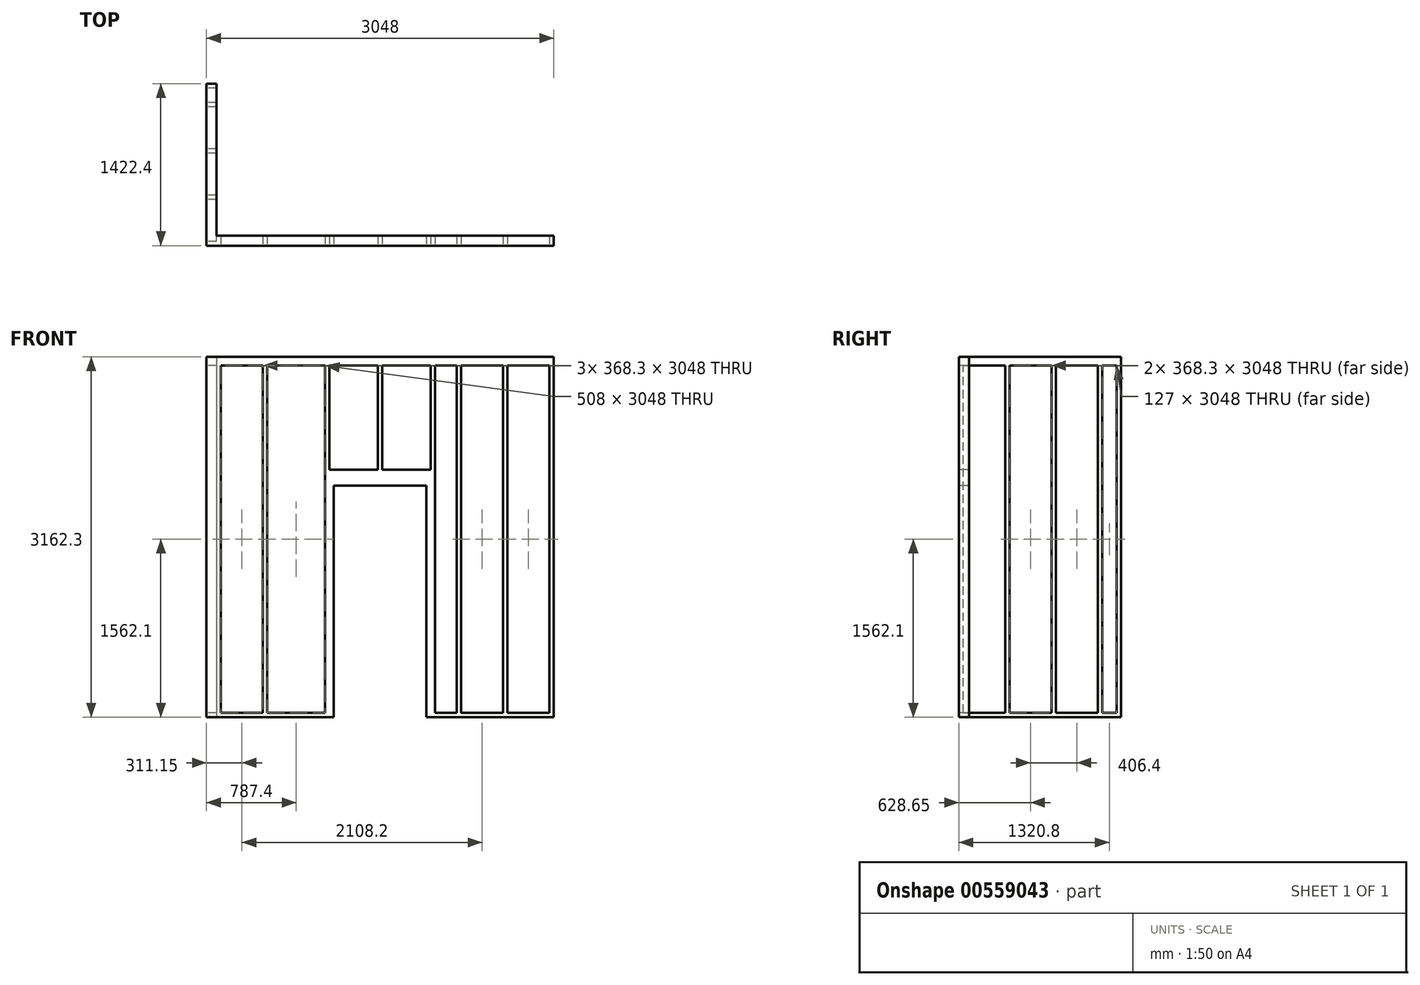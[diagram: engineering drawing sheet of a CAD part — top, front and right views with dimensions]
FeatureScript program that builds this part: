
annotation { "Feature Type Name" : "Feature", "Feature Type Description" : "" }
export const myFeature = defineFeature(function(context is Context, id is Id, definition is map)
    precondition{}
    {
        {
            var Q0;
            Q0=qCreatedBy(makeId("Top.planeOp"),FACE);
            var sketch = newSketch(context, id + "F0", { "sketchPlane" : qUnion([Q0])});
            skLineSegment(sketch, "E0", {"start": v(0, 0) * mm, "end": v(0, 1422.4) * mm});
            skLineSegment(sketch, "E1", {"start": v(0, 1422.4) * mm, "end": v(88.9, 1422.4) * mm});
            skLineSegment(sketch, "E2", {"start": v(88.9, 1422.4) * mm, "end": v(88.9, 88.9) * mm});
            skLineSegment(sketch, "E3", {"start": v(88.9, 88.9) * mm, "end": v(3048, 88.9) * mm});
            skLineSegment(sketch, "E4", {"start": v(3048, 88.9) * mm, "end": v(3048, 0) * mm});
            skLineSegment(sketch, "E5", {"start": v(3048, 0) * mm, "end": v(0, 0) * mm});
            skSolve(sketch);
        }
        {
            var Q0;
            Q0 = qSketchRegion(id + "F0", true);
            extrude(context, id + "F1", {"entities" : qUnion([Q0]), "depth" : 3162.3 * mm, "offsetDistance" : 25.4 * mm});
        }
        {
            var Q0;
            Q0=makeQuery(id+"F1.opExtrude","SWEPT_FACE",FACE,{"disambiguationData":[OSD([sQuery(id+"F0.wireOp",EDGE,"E0")])]});
            var sketch = newSketch(context, id + "F2", { "sketchPlane" : qUnion([Q0])});
            skLineSegment(sketch, "E6.bottom", {"start": v(-38.1, 38.1) * mm, "end": v(-406.4, 38.1) * mm});
            skLineSegment(sketch, "E6.top", {"start": v(-38.1, 3086.1) * mm, "end": v(-406.4, 3086.1) * mm});
            skLineSegment(sketch, "E6.left", {"start": v(-38.1, 38.1) * mm, "end": v(-38.1, 3086.1) * mm});
            skLineSegment(sketch, "E6.right", {"start": v(-406.4, 38.1) * mm, "end": v(-406.4, 3086.1) * mm});
            skLineSegment(sketch, "E7.bottom", {"start": v(-444.5, 38.1) * mm, "end": v(-812.8, 38.1) * mm});
            skLineSegment(sketch, "E7.top", {"start": v(-444.5, 3086.1) * mm, "end": v(-812.8, 3086.1) * mm});
            skLineSegment(sketch, "E7.left", {"start": v(-444.5, 38.1) * mm, "end": v(-444.5, 3086.1) * mm});
            skLineSegment(sketch, "E7.right", {"start": v(-812.8, 38.1) * mm, "end": v(-812.8, 3086.1) * mm});
            skLineSegment(sketch, "E8.bottom", {"start": v(-850.9, 38.1) * mm, "end": v(-1219.2, 38.1) * mm});
            skLineSegment(sketch, "E8.top", {"start": v(-850.9, 3086.1) * mm, "end": v(-1219.2, 3086.1) * mm});
            skLineSegment(sketch, "E8.left", {"start": v(-850.9, 38.1) * mm, "end": v(-850.9, 3086.1) * mm});
            skLineSegment(sketch, "E8.right", {"start": v(-1219.2, 38.1) * mm, "end": v(-1219.2, 3086.1) * mm});
            skLineSegment(sketch, "E9.bottom", {"start": v(-1384.3, 38.1) * mm, "end": v(-1257.3, 38.1) * mm});
            skLineSegment(sketch, "E9.top", {"start": v(-1384.3, 3086.1) * mm, "end": v(-1257.3, 3086.1) * mm});
            skLineSegment(sketch, "E9.left", {"start": v(-1384.3, 38.1) * mm, "end": v(-1384.3, 3086.1) * mm});
            skLineSegment(sketch, "E9.right", {"start": v(-1257.3, 38.1) * mm, "end": v(-1257.3, 3086.1) * mm});
            skSolve(sketch);
        }
        {
            var Q0;
            Q0 = qSketchRegion(id + "F2", true);
            extrude(context, id + "F3", {"entities" : qUnion([Q0]), "operationType" : NewBodyOperationType.REMOVE, "oppositeDirection" : true, "depth" : 88.9 * mm, "offsetDistance" : 25.4 * mm});
        }
        {
            var Q0;
            Q0=makeQuery(id+"F1.opExtrude","SWEPT_FACE",FACE,{"disambiguationData":[OSD([sQuery(id+"F0.wireOp",EDGE,"E5")])]});
            var sketch = newSketch(context, id + "F4", { "sketchPlane" : qUnion([Q0])});
            skLineSegment(sketch, "E10.bottom", {"start": v(1117.6, 0) * mm, "end": v(1930.4, 0) * mm});
            skLineSegment(sketch, "E10.top", {"start": v(1117.6, 2032) * mm, "end": v(1930.4, 2032) * mm});
            skLineSegment(sketch, "E10.left", {"start": v(1117.6, 0) * mm, "end": v(1117.6, 2032) * mm});
            skLineSegment(sketch, "E10.right", {"start": v(1930.4, 0) * mm, "end": v(1930.4, 2032) * mm});
            skLineSegment(sketch, "E11", {"start": v(1117.6, 0) * mm, "end": v(0, 0) * mm, "construction": true});
            skLineSegment(sketch, "E12", {"start": v(1930.4, 0) * mm, "end": v(3048, 0) * mm, "construction": true});
            skSolve(sketch);
        }
        {
            var Q0;
            Q0 = qSketchRegion(id + "F4", true);
            extrude(context, id + "F5", {"entities" : qUnion([Q0]), "operationType" : NewBodyOperationType.REMOVE, "endBound" : BoundingType.THROUGH_ALL, "oppositeDirection" : true, "depth" : 25.4 * mm, "offsetDistance" : 25.4 * mm});
        }
        {
            var Q0;
            Q0=makeQuery(id+"F1.opExtrude","SWEPT_FACE",FACE,{"disambiguationData":[OSD([sQuery(id+"F0.wireOp",EDGE,"E5")])]});
            var sketch = newSketch(context, id + "F6", { "sketchPlane" : qUnion([Q0])});
            skLineSegment(sketch, "E13.bottom", {"start": v(127, 38.1) * mm, "end": v(495.3, 38.1) * mm});
            skLineSegment(sketch, "E13.top", {"start": v(127, 3086.1) * mm, "end": v(495.3, 3086.1) * mm});
            skLineSegment(sketch, "E13.left", {"start": v(127, 38.1) * mm, "end": v(127, 3086.1) * mm});
            skLineSegment(sketch, "E13.right", {"start": v(495.3, 38.1) * mm, "end": v(495.3, 3086.1) * mm});
            skLineSegment(sketch, "E14.bottom", {"start": v(533.4, 38.1) * mm, "end": v(1041.4, 38.1) * mm});
            skLineSegment(sketch, "E14.top", {"start": v(533.4, 3086.1) * mm, "end": v(1041.4, 3086.1) * mm});
            skLineSegment(sketch, "E14.left", {"start": v(533.4, 38.1) * mm, "end": v(533.4, 3086.1) * mm});
            skLineSegment(sketch, "E14.right", {"start": v(1041.4, 38.1) * mm, "end": v(1041.4, 3086.1) * mm});
            skLineSegment(sketch, "E15.bottom", {"start": v(3009.9, 38.1) * mm, "end": v(2641.6, 38.1) * mm});
            skLineSegment(sketch, "E15.top", {"start": v(3009.9, 3086.1) * mm, "end": v(2641.6, 3086.1) * mm});
            skLineSegment(sketch, "E15.left", {"start": v(3009.9, 38.1) * mm, "end": v(3009.9, 3086.1) * mm});
            skLineSegment(sketch, "E15.right", {"start": v(2641.6, 38.1) * mm, "end": v(2641.6, 3086.1) * mm});
            skLineSegment(sketch, "E16.bottom", {"start": v(2603.5, 38.1) * mm, "end": v(2235.2, 38.1) * mm});
            skLineSegment(sketch, "E16.top", {"start": v(2603.5, 3086.1) * mm, "end": v(2235.2, 3086.1) * mm});
            skLineSegment(sketch, "E16.left", {"start": v(2603.5, 38.1) * mm, "end": v(2603.5, 3086.1) * mm});
            skLineSegment(sketch, "E16.right", {"start": v(2235.2, 38.1) * mm, "end": v(2235.2, 3086.1) * mm});
            skLineSegment(sketch, "E17.bottom", {"start": v(2197.1, 38.1) * mm, "end": v(2006.6, 38.1) * mm});
            skLineSegment(sketch, "E17.top", {"start": v(2197.1, 3086.1) * mm, "end": v(2006.6, 3086.1) * mm});
            skLineSegment(sketch, "E17.left", {"start": v(2197.1, 38.1) * mm, "end": v(2197.1, 3086.1) * mm});
            skLineSegment(sketch, "E17.right", {"start": v(2006.6, 38.1) * mm, "end": v(2006.6, 3086.1) * mm});
            skLineSegment(sketch, "E18.bottom", {"start": v(1079.5, 2171.7) * mm, "end": v(1504.95, 2171.7) * mm});
            skLineSegment(sketch, "E18.top", {"start": v(1079.5, 3086.1) * mm, "end": v(1504.95, 3086.1) * mm});
            skLineSegment(sketch, "E18.left", {"start": v(1079.5, 2171.7) * mm, "end": v(1079.5, 3086.1) * mm});
            skLineSegment(sketch, "E18.right", {"start": v(1504.95, 2171.7) * mm, "end": v(1504.95, 3086.1) * mm});
            skLineSegment(sketch, "E19.bottom", {"start": v(1968.5, 3086.1) * mm, "end": v(1543.05, 3086.1) * mm});
            skLineSegment(sketch, "E19.top", {"start": v(1968.5, 2171.7) * mm, "end": v(1543.05, 2171.7) * mm});
            skLineSegment(sketch, "E19.left", {"start": v(1968.5, 3086.1) * mm, "end": v(1968.5, 2171.7) * mm});
            skLineSegment(sketch, "E19.right", {"start": v(1543.05, 3086.1) * mm, "end": v(1543.05, 2171.7) * mm});
            skSolve(sketch);
        }
        {
            var Q0;
            Q0 = qSketchRegion(id + "F6", true);
            extrude(context, id + "F7", {"entities" : qUnion([Q0]), "operationType" : NewBodyOperationType.REMOVE, "oppositeDirection" : true, "depth" : 88.9 * mm, "offsetDistance" : 25.4 * mm});
        }
    });
